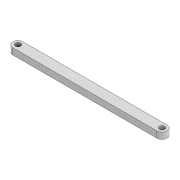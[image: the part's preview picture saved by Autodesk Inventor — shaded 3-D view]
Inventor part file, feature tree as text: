
AUTODESK INVENTOR PART (.ipt)
format: ipt  version: 2022 (Build 260153000, 153)  size: 90,624 bytes
history: native  units: mm
features: extrude x1
ambient origin geometry x8: Origin, YZ Plane, XZ Plane, XY Plane, X Axis, Y Axis, Z Axis, Center Point
bodies: Solid1 (feature_tree)
feature tree (1):
  extrude  "Extrusion1"  Depth=112.547mm
